# Revit family: Sink-Kitchen-KOHLER-Verse-K-20060
name_source: partatom
category: Plumbing Fixtures
revit_build: Autodesk Revit 2015 (Build: 20140606_1530(x64)
units: mm (PartAtom-declared; Revit-internal decimal feet)

## types (3) — shared parameters
ADA Compliant = No
Assembly Code = D2010400
CW Connection = No
Cold Water Inlet = Cold Water Inlet
Date Modified = 4/19/2018
Default Elevation = 36"
Drain Included = No
Finish = Kohler-Metal-NA-Stainless
HW Connection = No
Height = 9 5/16"
Hot Water Inlet = Hot Water Inlet
Length = 22"
Manufacturer = KOHLER Co.
MasterFormat 1995 = 15410
MasterFormat 2004 = 22.41.16
Material = Stainless Steel
Product Documentation Link = http://www.us.kohler.com
Product Name = Verse
Product Page URL = http://www.us.kohler.com
URL = https://www.us.kohler.com
Vent Connection = No
Waste Connection = Yes
Waste Water Outlet = Waste Water Outlet
Width = 33"

## per-type parameters (varying)
| type | 3 Faucet Hole | 4 Faucet Hole | Description | Model | Type |
| Single Faucet Hole Kitchen Sink | No | No | 33inch x 22inch x 9inch top-mount single-bowl kitchen sink with single faucet hole | K-20060-1-NA | 1 |
| 3 Faucet Hole Kitchen Sink | Yes | No | 33inch x 22inch x 9inch top-mount single-bowl kitchen sink with 3 faucet hole | K-20060-3-NA | 2 |
| 4 Faucet Hole Kitchen Sink | No | Yes | 33inch x 22inch x 9inch top-mount single-bowl kitchen sink with 4 faucet hole | K-20060-4-NA | 3 |

## geometry (parser evidence)
native form markers: Blend x4, Sweep x2
no freeform markers — native parametric forms only
